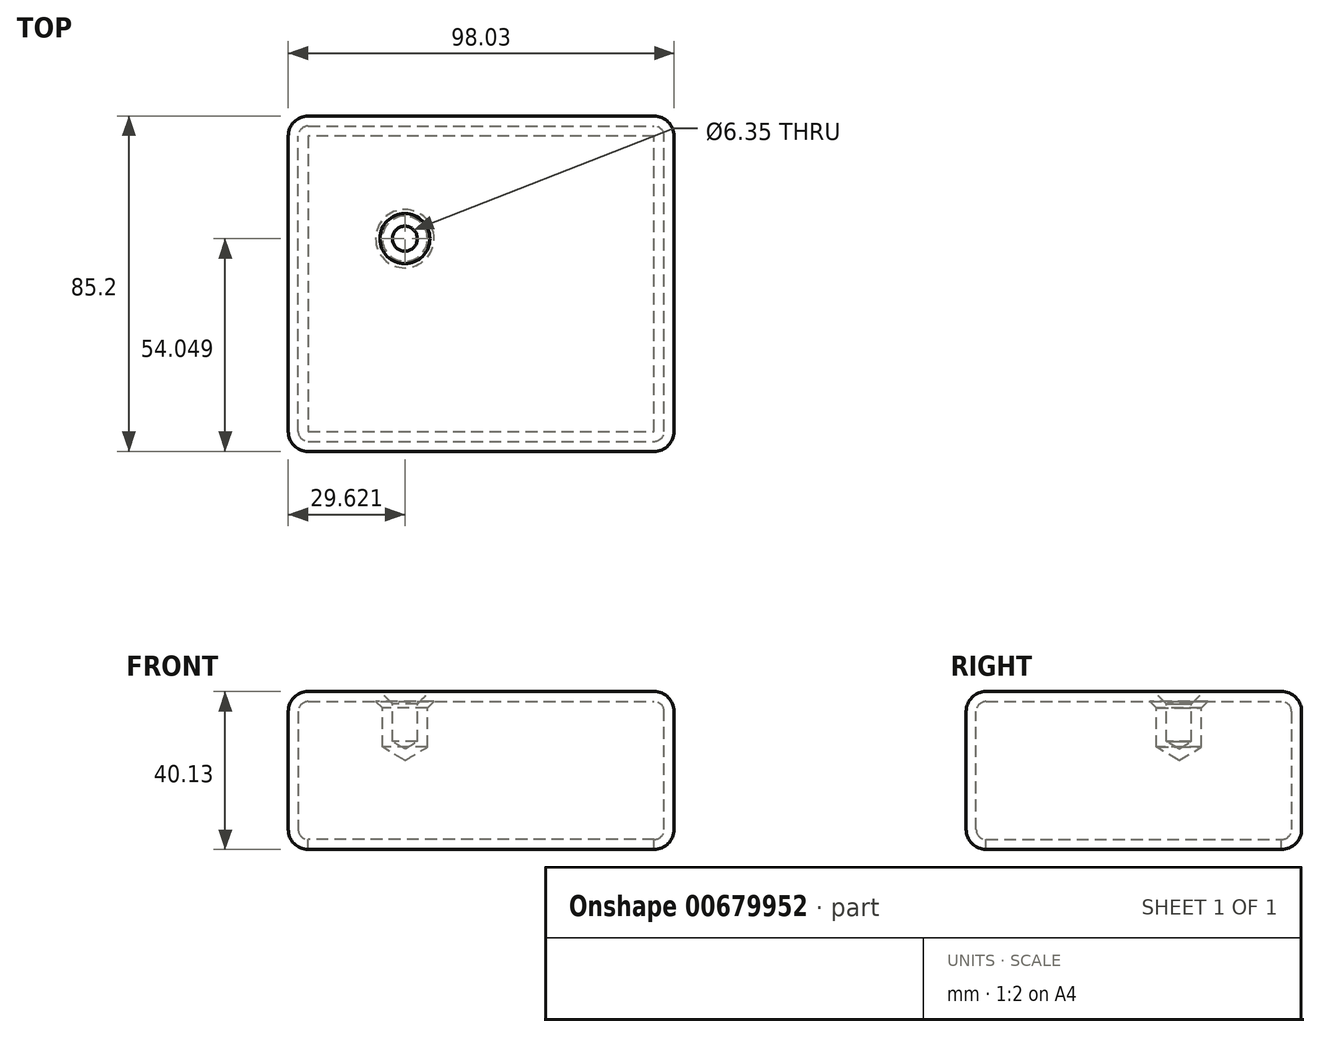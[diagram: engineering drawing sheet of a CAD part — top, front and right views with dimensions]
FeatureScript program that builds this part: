
annotation { "Feature Type Name" : "Feature", "Feature Type Description" : "" }
export const myFeature = defineFeature(function(context is Context, id is Id, definition is map)
    precondition{}
    {
        {
            var Q0;
            Q0=qCreatedBy(makeId("Top.planeOp"),FACE);
            var sketch = newSketch(context, id + "F0", { "sketchPlane" : qUnion([Q0])});
            skLineSegment(sketch, "E0", {"start": v(-47.18, 48.7) * mm, "end": v(-47.18, -36.5) * mm});
            skLineSegment(sketch, "E1", {"start": v(-47.18, -36.5) * mm, "end": v(50.85, -36.5) * mm});
            skLineSegment(sketch, "E2", {"start": v(50.85, -36.5) * mm, "end": v(50.85, 48.7) * mm});
            skLineSegment(sketch, "E3", {"start": v(50.85, 48.7) * mm, "end": v(-47.18, 48.7) * mm});
            skSolve(sketch);
        }
        {
            var Q0;
            Q0 = qSketchRegion(id + "F0", true);
            extrude(context, id + "F1", {"entities" : qUnion([Q0]), "depth" : 40.13 * mm, "offsetDistance" : 25.4 * mm});
        }
        {
            var Q0;
            Q0=makeQuery(id+"F1.opExtrude","CAP_FACE",FACE,{"disambiguationData":[OSD([sQuery(id+"F0.wireOp",EDGE,"E0"),sQuery(id+"F0.wireOp",EDGE,"E1"),sQuery(id+"F0.wireOp",EDGE,"E2"),sQuery(id+"F0.wireOp",EDGE,"E3")])],"isStart":false});
            var Q1;
            Q1=makeQuery(id+"F1.opExtrude","SWEPT_FACE",FACE,{"disambiguationData":[OSD([sQuery(id+"F0.wireOp",EDGE,"E2")])]});
            var Q2;
            Q2=makeQuery(id+"F1.opExtrude","SWEPT_FACE",FACE,{"disambiguationData":[OSD([sQuery(id+"F0.wireOp",EDGE,"E1")])]});
            var Q3;
            Q3=makeQuery(id+"F1.opExtrude","SWEPT_FACE",FACE,{"disambiguationData":[OSD([sQuery(id+"F0.wireOp",EDGE,"E3")])]});
            var Q4;
            Q4=makeQuery(id+"F1.opExtrude","SWEPT_FACE",FACE,{"disambiguationData":[OSD([sQuery(id+"F0.wireOp",EDGE,"E0")])]});
            fillet(context, id + "F2", {"entities" : qUnion([Q0, Q1, Q2, Q3, Q4]), "radius" : 5.08 * mm, "tangentPropagation" : true, "allowEdgeOverflow" : false});
        }
        {
            var Q0;
            Q0=makeQuery(id+"F1.opExtrude","CAP_FACE",FACE,{"disambiguationData":[OSD([sQuery(id+"F0.wireOp",EDGE,"E0"),sQuery(id+"F0.wireOp",EDGE,"E1"),sQuery(id+"F0.wireOp",EDGE,"E2"),sQuery(id+"F0.wireOp",EDGE,"E3")])],"isStart":false});
            var sketch = newSketch(context, id + "F3", { "sketchPlane" : qUnion([Q0])});
            skCircle(sketch, "E4", {"center": v(-17.56, 17.56) * mm, "radius": 8.74 * mm});
            skSolve(sketch);
        }
        {
            var Q0;
            Q0=sQuery(id+"F3.wireOp",VERTEX,"E4.center");
            var Q1;
            Q1=makeQuery(id+"F1.opExtrude","SWEPT_BODY",BODY,{"disambiguationData":[OSD([sQuery(id+"F0.wireOp",EDGE,"E0"),sQuery(id+"F0.wireOp",EDGE,"E1"),sQuery(id+"F0.wireOp",EDGE,"E2"),sQuery(id+"F0.wireOp",EDGE,"E3")])]});
            hole(context, id + "F4", {"style" : HoleStyle.C_SINK, "endStyle" : HoleEndStyle.BLIND, "holeDiameter" : 6.35 * mm, "cSinkDiameter" : 12.7 * mm, "cSinkAngle" : 90 * degree, "majorDiameter" : 6.35 * mm, "holeDepth" : 12.7 * mm, "isTappedThrough" : true, "tappedDepth" : 12.7 * mm, "tapClearance" : 3, "locations" : qUnion([Q0]), "scope" : qUnion([Q1])});
        }
        {
            var Q0;
            Q0=makeQuery(id+"F1.opExtrude","CAP_FACE",FACE,{"disambiguationData":[OSD([sQuery(id+"F0.wireOp",EDGE,"E0"),sQuery(id+"F0.wireOp",EDGE,"E1"),sQuery(id+"F0.wireOp",EDGE,"E2"),sQuery(id+"F0.wireOp",EDGE,"E3")])],"isStart":true});
            shell(context, id + "F5", {"entities" : qUnion([Q0]), "thickness" : 2.54 * mm});
        }
    });
